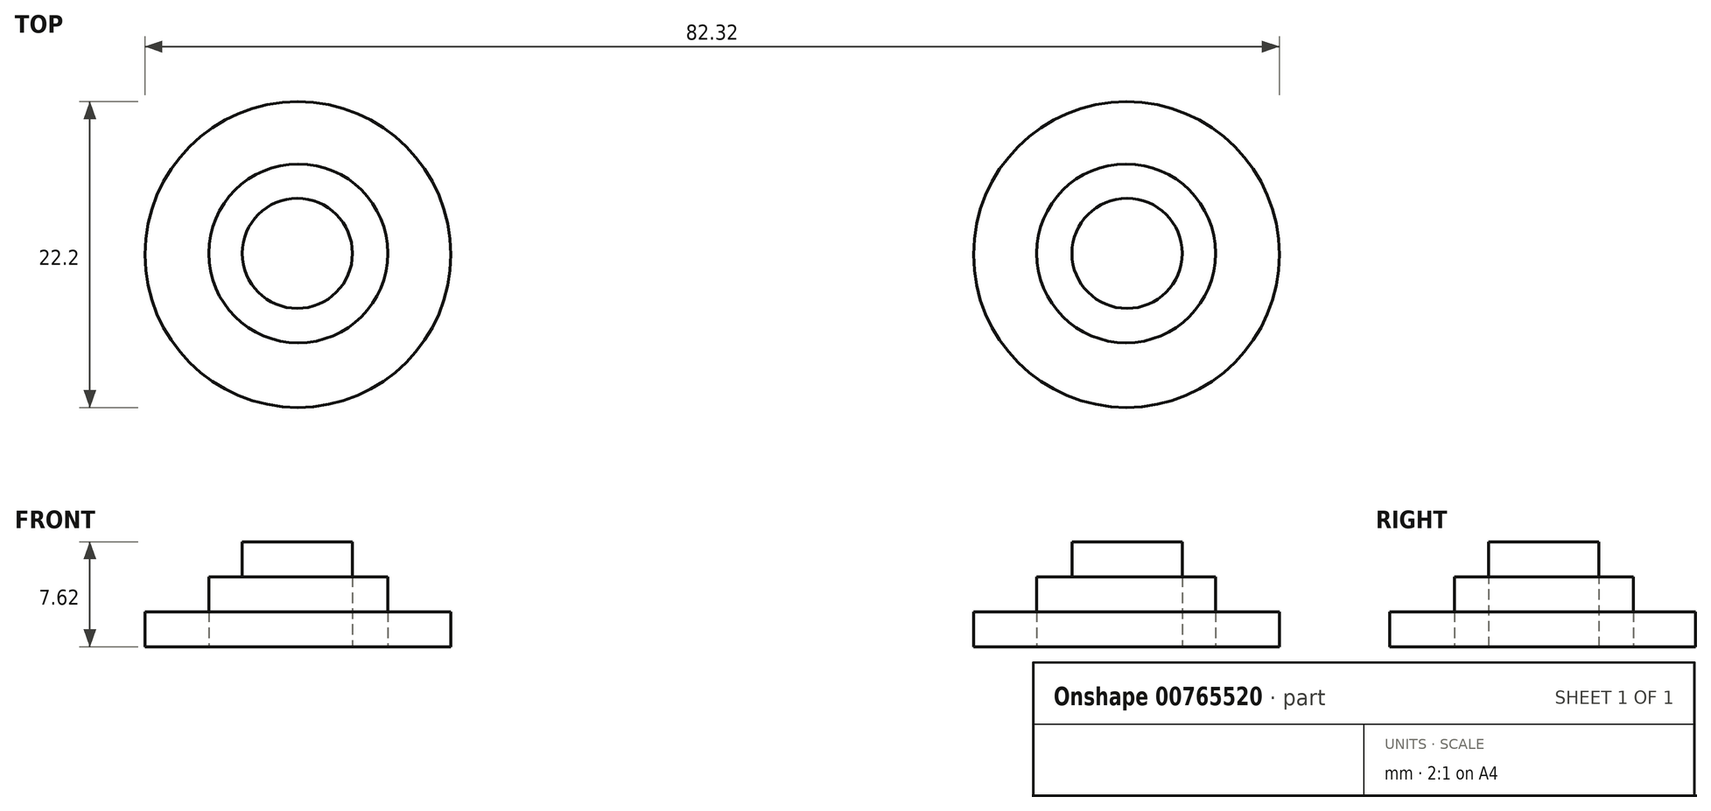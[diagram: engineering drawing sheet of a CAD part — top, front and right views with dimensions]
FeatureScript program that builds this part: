
annotation { "Feature Type Name" : "Feature", "Feature Type Description" : "" }
export const myFeature = defineFeature(function(context is Context, id is Id, definition is map)
    precondition{}
    {
        {
            var Q0;
            Q0=qCreatedBy(makeId("Top.planeOp"),FACE);
            var sketch = newSketch(context, id + "F0", { "sketchPlane" : qUnion([Q0])});
            skCircle(sketch, "E0", {"center": v(-30.07, -0.09) * mm, "radius": 11.1 * mm});
            skCircle(sketch, "E1.MirrorC", {"center": v(30.07, -0.09) * mm, "radius": 11.1 * mm});
            skSolve(sketch);
        }
        {
            var Q0;
            Q0 = qSketchRegion(id + "F0", true);
            extrude(context, id + "F1", {"entities" : qUnion([Q0]), "depth" : 2.54 * mm, "offsetDistance" : 25.4 * mm});
        }
        {
            var Q0;
            Q0=qCreatedBy(makeId("Top.planeOp"),FACE);
            var sketch = newSketch(context, id + "F2", { "sketchPlane" : qUnion([Q0])});
            skCircle(sketch, "E2", {"center": v(-30.04, 0) * mm, "radius": 6.5 * mm});
            skCircle(sketch, "E3.MirrorC", {"center": v(30.04, 0) * mm, "radius": 6.5 * mm});
            skSolve(sketch);
        }
        {
            var Q0;
            Q0 = qSketchRegion(id + "F2", true);
            extrude(context, id + "F3", {"entities" : qUnion([Q0]), "depth" : 5.08 * mm, "offsetDistance" : 25.4 * mm});
        }
        {
            var Q0;
            Q0=qCreatedBy(makeId("Top.planeOp"),FACE);
            var sketch = newSketch(context, id + "F4", { "sketchPlane" : qUnion([Q0])});
            skCircle(sketch, "E4", {"center": v(-30.1, 0) * mm, "radius": 4 * mm});
            skCircle(sketch, "E5.MirrorC", {"center": v(30.1, 0) * mm, "radius": 4 * mm});
            skSolve(sketch);
        }
        {
            var Q0;
            Q0 = qSketchRegion(id + "F4", true);
            extrude(context, id + "F5", {"entities" : qUnion([Q0]), "depth" : 7.62 * mm, "offsetDistance" : 25.4 * mm});
        }
    });
